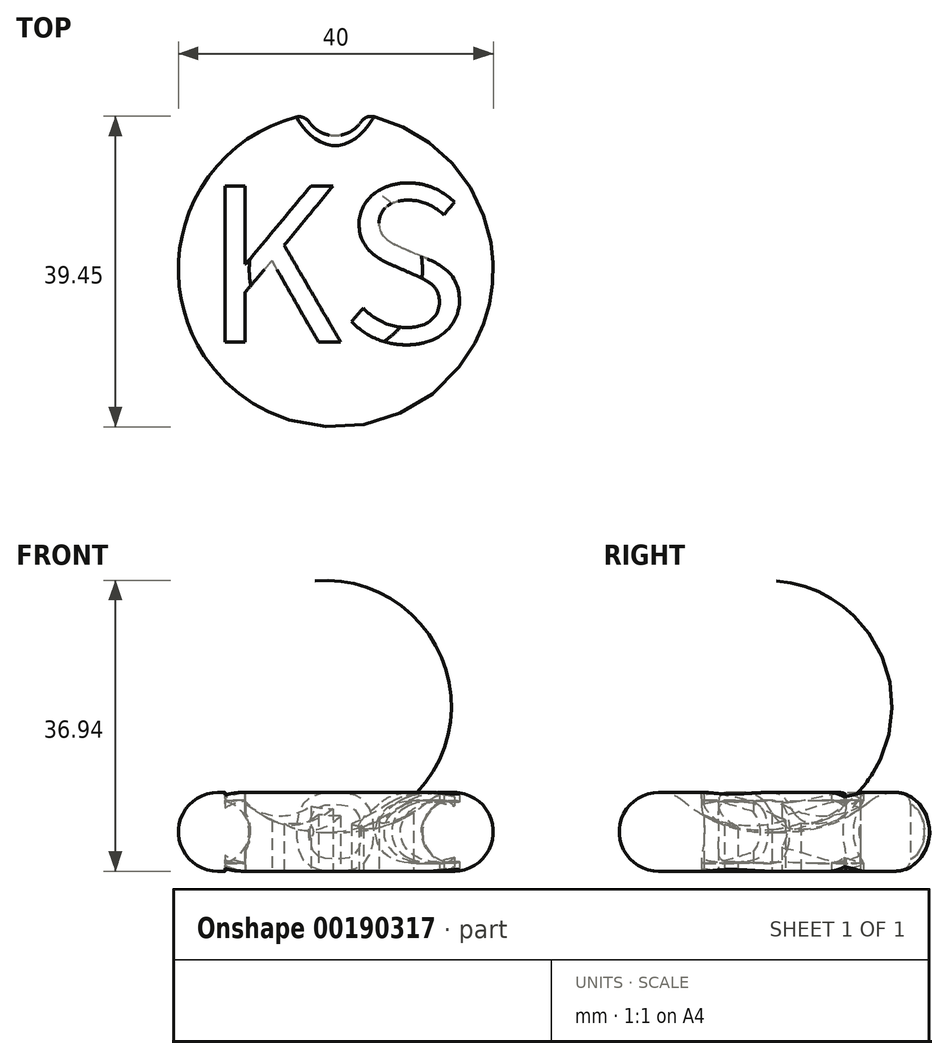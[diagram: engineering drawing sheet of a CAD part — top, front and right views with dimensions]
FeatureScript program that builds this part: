
annotation { "Feature Type Name" : "Feature", "Feature Type Description" : "" }
export const myFeature = defineFeature(function(context is Context, id is Id, definition is map)
    precondition{}
    {
        {
            var Q0;
            Q0=qCreatedBy(makeId("Front.planeOp"),FACE);
            var sketch = newSketch(context, id + "F0", { "sketchPlane" : qUnion([Q0])});
            skArc(sketch, "E0", {"start": v(-11.75, 8.8) * mm, "mid": v(-19.69, 6.73) * mm, "end": v(-15, 0) * mm});
            skArc(sketch, "E1", {"start": v(-11.75, 8.8) * mm, "mid": v(-6.25, 5.72) * mm, "end": v(0, 5) * mm});
            skLineSegment(sketch, "E2", {"start": v(-15, 0) * mm, "end": v(0, 0) * mm});
            skLineSegment(sketch, "E3", {"start": v(0, 0) * mm, "end": v(0, 5) * mm});
            skSolve(sketch);
        }
        {
            var Q0;
            Q0=qCreatedBy(makeId("Top.planeOp"),FACE);
            var sketch = newSketch(context, id + "F1", { "sketchPlane" : qUnion([Q0])});
            skText(sketch, "E4", { "text": "KS\n", "fontName": "NotoSansCJKjp-Regular.otf"});
            const initialGuessF1  = {"E4": [-0.01677, -0.00923, 1, 0, 0.0195]};
            skSetInitialGuess(sketch, initialGuessF1);
            skSolve(sketch);
        }
        {
            var Q0;
            Q0=makeQuery(id+"F0.imprint","IMPRINT",FACE,{"disambiguationData":[TD([[makeQuery(id+"F0.imprint","IMPRINT",EDGE,{"derivedFrom":sQuery(id+"F0.wireOp",EDGE,"E0")}),1.0]])]});
            var Q1;
            Q1=sQuery(id+"F0.wireOp",EDGE,"E3");
            revolve(context, id + "F2", {"entities" : qUnion([Q0]), "axis" : qUnion([Q1]), "revolveType" : RevolveType.FULL});
        }
        {
            var Q0;
            Q0 = qSketchRegion(id + "F1", true);
            extrude(context, id + "F3", {"entities" : qUnion([Q0]), "operationType" : NewBodyOperationType.REMOVE, "depth" : 25 * mm});
        }
        {
            var Q0;
            Q0=qCreatedBy(makeId("Front.planeOp"),FACE);
            var sketch = newSketch(context, id + "F4", { "sketchPlane" : qUnion([Q0])});
            skCircle(sketch, "E5", {"center": v(-15, 5) * mm, "radius": 4 * mm});
            skSolve(sketch);
        }
        {
            var Q0;
            Q0 = qSketchRegion(id + "F4", true);
            var Q1;
            Q1=sQuery(id+"F0.wireOp",EDGE,"E3");
            revolve(context, id + "F5", {"operationType" : NewBodyOperationType.ADD, "entities" : qUnion([Q0]), "axis" : qUnion([Q1]), "revolveType" : RevolveType.FULL});
        }
        {
            var Q0;
            Q0=qCreatedBy(makeId("Top.planeOp"),FACE);
            var sketch = newSketch(context, id + "F6", { "sketchPlane" : qUnion([Q0])});
            skCircle(sketch, "E6", {"center": v(-0.1, 21) * mm, "radius": 4 * mm});
            skSolve(sketch);
        }
        {
            var Q0;
            Q0 = qSketchRegion(id + "F6", true);
            extrude(context, id + "F7", {"entities" : qUnion([Q0]), "operationType" : NewBodyOperationType.REMOVE, "depth" : 25 * mm});
        }
        {
            var Q0;
            Q0=makeQuery(id+"F7.boolean.opBoolean","INTERSECT",EDGE,{"derivedFrom":[makeQuery(id+"F3.boolean.opBoolean","SPLIT",FACE,{"disambiguationData":[TD([makeQuery(id+"F2.opRevolve","SWEPT_FACE",FACE,{"disambiguationData":[OSD([sQuery(id+"F0.wireOp",EDGE,"E2")])]})])],"derivedFrom":makeQuery(id+"F2.opRevolve","SWEPT_FACE",FACE,{"disambiguationData":[OSD([sQuery(id+"F0.wireOp",EDGE,"E0")])]})}),makeQuery(id+"F7.opExtrude","SWEPT_FACE",FACE,{"disambiguationData":[OSD([sQuery(id+"F6.wireOp",EDGE,"E6")])]})]});
            fillet(context, id + "F8", {"entities" : qUnion([Q0]), "radius" : 1.5 * mm, "tangentPropagation" : true, "allowEdgeOverflow" : false});
        }
    });
